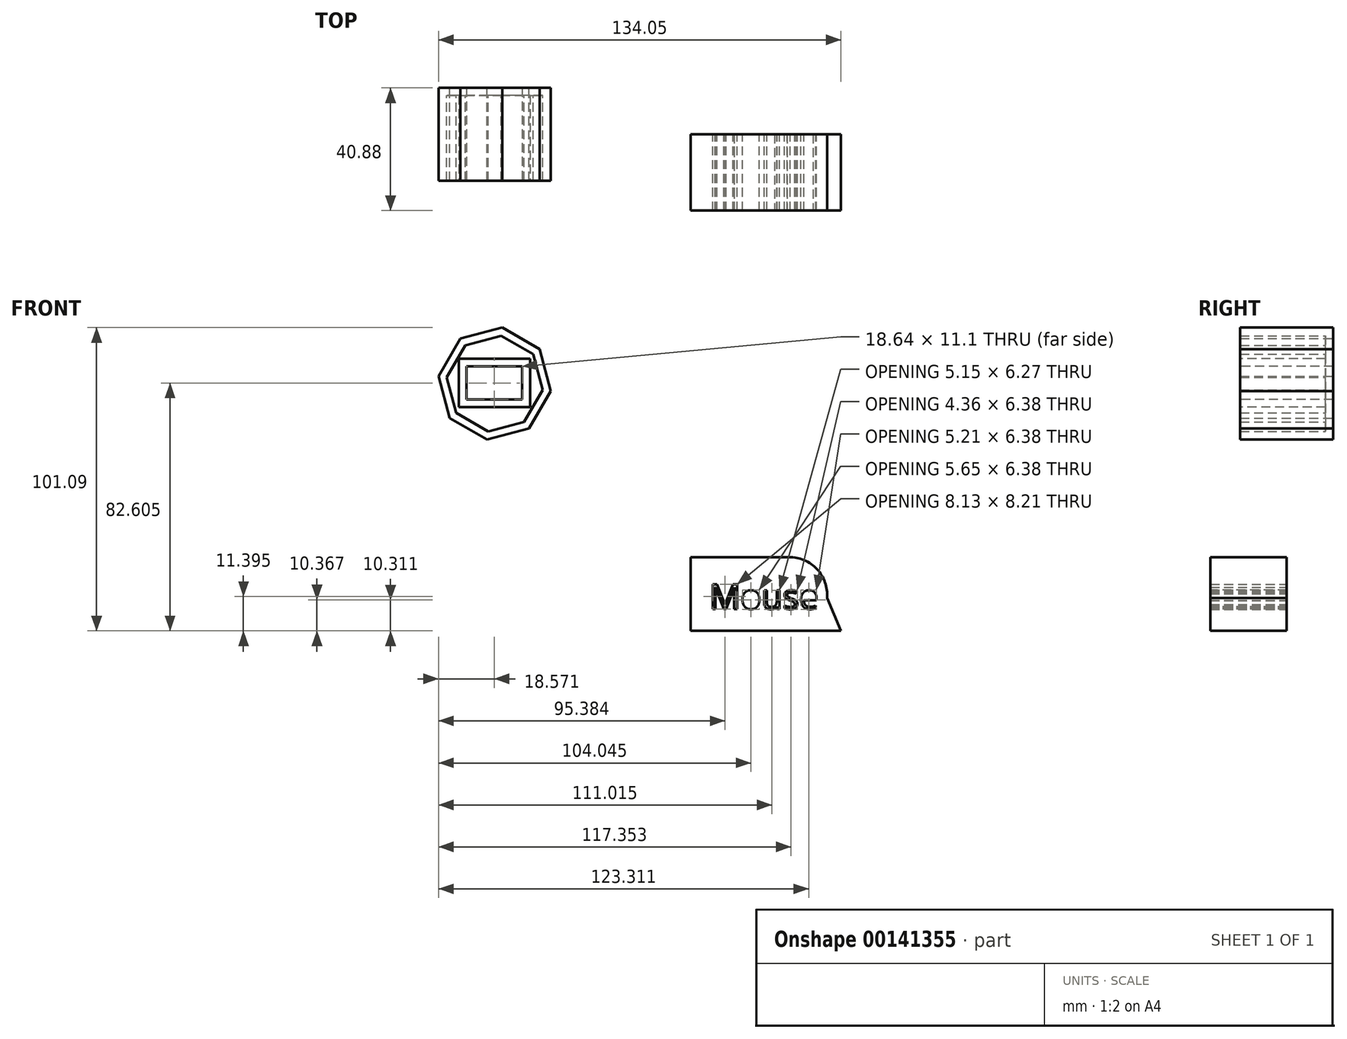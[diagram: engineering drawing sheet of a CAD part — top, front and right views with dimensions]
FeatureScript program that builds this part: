
annotation { "Feature Type Name" : "Feature", "Feature Type Description" : "" }
export const myFeature = defineFeature(function(context is Context, id is Id, definition is map)
    precondition{}
    {
        {
            var Q0;
            Q0=qCreatedBy(makeId("Front.planeOp"),FACE);
            var sketch = newSketch(context, id + "F0", { "sketchPlane" : qUnion([Q0])});
            skLineSegment(sketch, "E0", {"start": v(-48.09, 46.5) * mm, "end": v(-48.09, 0) * mm});
            skLineSegment(sketch, "E1", {"start": v(-48.09, 0) * mm, "end": v(-1.65, 2.43) * mm});
            skLineSegment(sketch, "E2", {"start": v(23.5, 46.5) * mm, "end": v(23.5, 0) * mm});
            skLineSegment(sketch, "E3", {"start": v(49.87, 46.5) * mm, "end": v(49.87, 0) * mm});
            skLineSegment(sketch, "E4.bottom", {"start": v(-36.53, -25) * mm, "end": v(-3.77, -25) * mm});
            skLineSegment(sketch, "E4.top", {"start": v(-36.53, -49.6) * mm, "end": v(13.55, -49.6) * mm});
            skLineSegment(sketch, "E4.left", {"start": v(-36.53, -25) * mm, "end": v(-36.53, -37.3) * mm});
            skLineSegment(sketch, "E4.right", {"start": v(8.9, -38.64) * mm, "end": v(13.54, -49.6) * mm});
            skPoint(sketch, "E5.visualSharp", {"position": v(13.55, -25) * mm});
            skArc(sketch, "E5.filletArc", {"start": v(8.9, -38.64) * mm, "mid": v(5.54, -29.05) * mm, "end": v(-3.77, -25) * mm});
            skLineSegment(sketch, "E6", {"start": v(-36.53, -37.3) * mm, "end": v(-36.53, -49.6) * mm});
            skText(sketch, "E7", { "text": "Mouse\n", "fontName": "OpenSans-Regular.ttf"});
            skArc(sketch, "E8", {"start": v(-36.53, -25) * mm, "mid": v(-57.7, -16.45) * mm, "end": v(-48.4, -37.3) * mm});
            skCircle(sketch, "E9.cCircle", {"center": v(-101.82, 32.82) * mm, "radius": 17.41 * mm, "construction": true});
            skLineSegment(sketch, "E9.0", {"start": v(-83.14, 30.33) * mm, "end": v(-90.37, 17.85) * mm});
            skLineSegment(sketch, "E9.1", {"start": v(-90.37, 17.85) * mm, "end": v(-104.3, 14.13) * mm});
            skLineSegment(sketch, "E9.2", {"start": v(-104.3, 14.13) * mm, "end": v(-116.79, 21.36) * mm});
            skLineSegment(sketch, "E9.3", {"start": v(-116.79, 21.36) * mm, "end": v(-120.5, 35.3) * mm});
            skLineSegment(sketch, "E9.4", {"start": v(-120.5, 35.3) * mm, "end": v(-113.28, 47.78) * mm});
            skLineSegment(sketch, "E9.5", {"start": v(-113.28, 47.78) * mm, "end": v(-99.34, 51.5) * mm});
            skLineSegment(sketch, "E9.6", {"start": v(-99.34, 51.5) * mm, "end": v(-86.85, 44.27) * mm});
            skLineSegment(sketch, "E9.7", {"start": v(-86.85, 44.27) * mm, "end": v(-83.14, 30.33) * mm});
            skPoint(sketch, "E9.0.midPoint", {"position": v(-86.75, 24.1) * mm});
            skCircle(sketch, "E10.cCircle", {"center": v(-128, 9.34) * mm, "radius": 10.35 * mm, "construction": true});
            skLineSegment(sketch, "E10.0", {"start": v(-128, -1.01) * mm, "end": v(-136.97, 14.5) * mm});
            skLineSegment(sketch, "E10.1", {"start": v(-136.97, 14.5) * mm, "end": v(-119.05, 14.5) * mm});
            skLineSegment(sketch, "E10.2", {"start": v(-119.05, 14.5) * mm, "end": v(-128, -1.01) * mm});
            const initialGuessF0  = {"E7": [-0.03032, -0.0423, 1, 0, 0.00828]};
            skSetInitialGuess(sketch, initialGuessF0);
            skSolve(sketch);
        }
        {
            var Q0;
            Q0=makeQuery(id+"F0.imprint","IMPRINT",FACE,{"disambiguationData":[TD([[makeQuery(id+"F0.imprint","IMPRINT",EDGE,{"derivedFrom":sQuery(id+"F0.wireOp",EDGE,"E4.bottom")}),-1.0]])]});
            extrude(context, id + "F1", {"entities" : qUnion([Q0]), "depth" : 25.4 * mm});
        }
        {
            var Q0;
            Q0=makeQuery(id+"F0.imprint","IMPRINT",FACE,{"disambiguationData":[TD([[makeQuery(id+"F0.imprint","IMPRINT",EDGE,{"derivedFrom":sQuery(id+"F0.wireOp",EDGE,"E9.0")}),-1.0]])]});
            extrude(context, id + "F2", {"entities" : qUnion([Q0]), "endBound" : BoundingType.SYMMETRIC, "depth" : 30.95 * mm});
        }
        {
            var Q0;
            Q0=makeQuery(id+"F2.opExtrude","CAP_FACE",FACE,{"disambiguationData":[OSD([sQuery(id+"F0.wireOp",EDGE,"E9.0"),sQuery(id+"F0.wireOp",EDGE,"E9.1"),sQuery(id+"F0.wireOp",EDGE,"E9.2"),sQuery(id+"F0.wireOp",EDGE,"E9.3"),sQuery(id+"F0.wireOp",EDGE,"E9.4"),sQuery(id+"F0.wireOp",EDGE,"E9.5"),sQuery(id+"F0.wireOp",EDGE,"E9.6"),sQuery(id+"F0.wireOp",EDGE,"E9.7")])],"isStart":false});
            var sketch = newSketch(context, id + "F3", { "sketchPlane" : qUnion([Q0])});
            skLineSegment(sketch, "E11.bottom", {"start": v(-111.26, 38.57) * mm, "end": v(-92.62, 38.57) * mm});
            skLineSegment(sketch, "E11.top", {"start": v(-111.26, 27.46) * mm, "end": v(-92.62, 27.46) * mm});
            skLineSegment(sketch, "E11.left", {"start": v(-111.26, 38.57) * mm, "end": v(-111.26, 27.46) * mm});
            skLineSegment(sketch, "E11.right", {"start": v(-92.62, 38.57) * mm, "end": v(-92.62, 27.46) * mm});
            skPoint(sketch, "E11.middle", {"position": v(-101.94, 33.02) * mm});
            skSolve(sketch);
        }
        {
            var Q0;
            Q0 = qSketchRegion(id + "F3", true);
            extrude(context, id + "F4", {"entities" : qUnion([Q0]), "operationType" : NewBodyOperationType.REMOVE, "endBound" : BoundingType.UP_TO_NEXT, "oppositeDirection" : true, "depth" : 25.4 * mm});
        }
        {
            var Q0;
            Q0=makeQuery(id+"F2.opExtrude","CAP_FACE",FACE,{"disambiguationData":[OSD([sQuery(id+"F0.wireOp",EDGE,"E9.0"),sQuery(id+"F0.wireOp",EDGE,"E9.1"),sQuery(id+"F0.wireOp",EDGE,"E9.2"),sQuery(id+"F0.wireOp",EDGE,"E9.3"),sQuery(id+"F0.wireOp",EDGE,"E9.4"),sQuery(id+"F0.wireOp",EDGE,"E9.5"),sQuery(id+"F0.wireOp",EDGE,"E9.6"),sQuery(id+"F0.wireOp",EDGE,"E9.7")])],"isStart":false});
            shell(context, id + "F5", {"entities" : qUnion([Q0]), "thickness" : 2.54 * mm});
        }
    });
